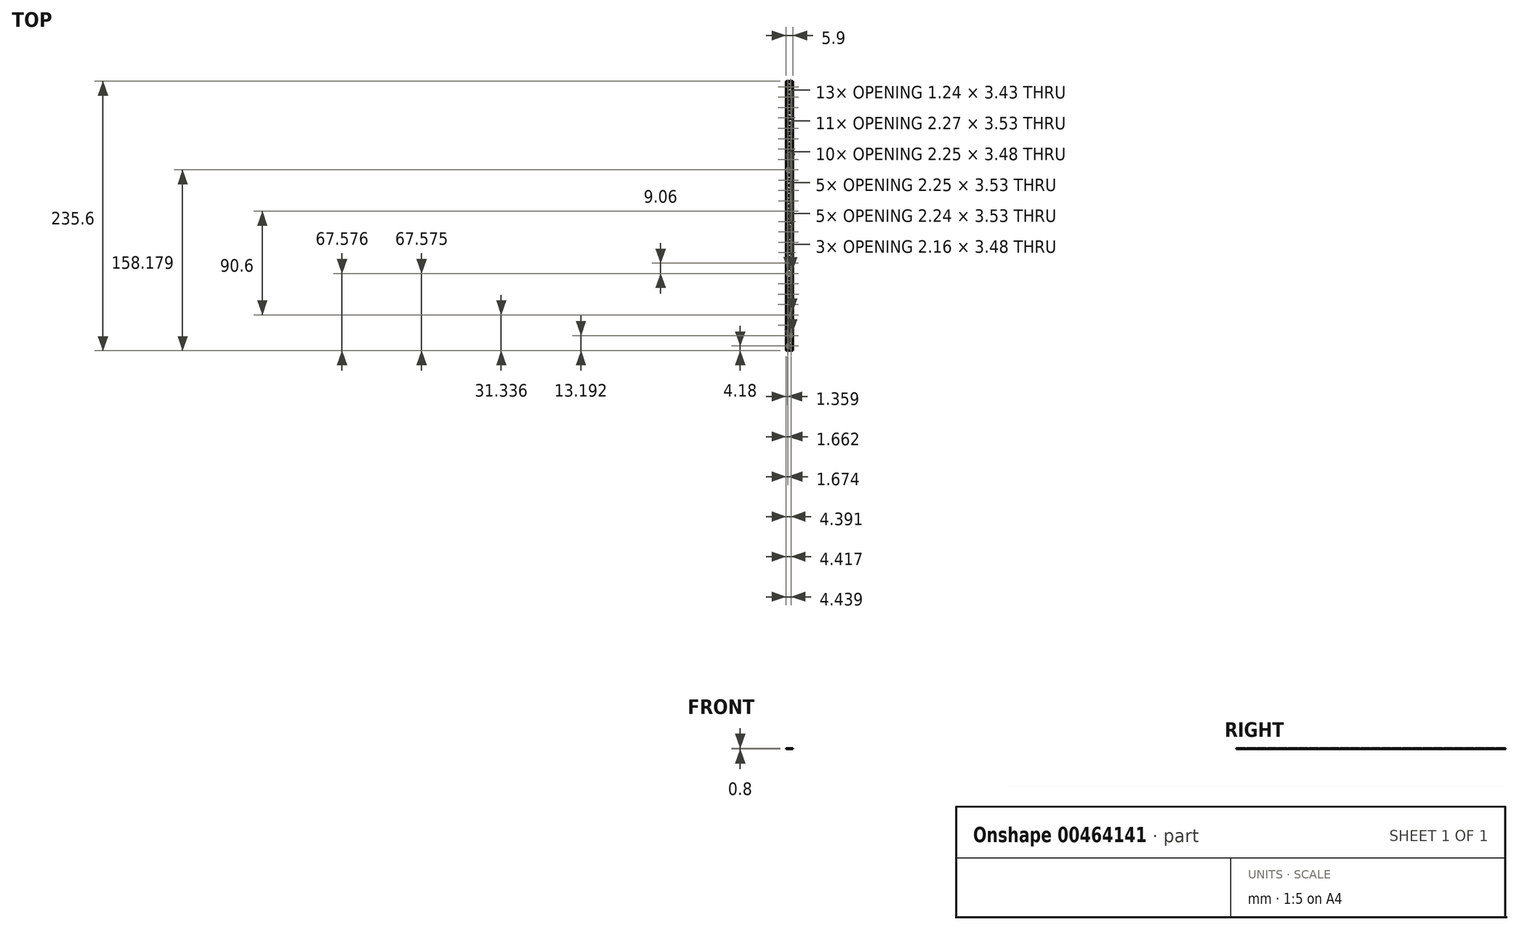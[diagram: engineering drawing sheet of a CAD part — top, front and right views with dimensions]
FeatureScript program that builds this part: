
annotation { "Feature Type Name" : "Feature", "Feature Type Description" : "" }
export const myFeature = defineFeature(function(context is Context, id is Id, definition is map)
    precondition{}
    {
        {
            var Q0;
            Q0=qCreatedBy(makeId("Top.planeOp"),FACE);
            var sketch = newSketch(context, id + "F0", { "sketchPlane" : qUnion([Q0])});
            skLineSegment(sketch, "E0.bottom", {"start": v(0, 0) * mm, "end": v(7.5, 0) * mm});
            skLineSegment(sketch, "E0.top", {"start": v(0, -235.6) * mm, "end": v(7.5, -235.6) * mm});
            skLineSegment(sketch, "E0.left", {"start": v(0, 0) * mm, "end": v(0, -235.6) * mm});
            skLineSegment(sketch, "E0.right", {"start": v(7.5, 0) * mm, "end": v(7.5, -235.6) * mm});
            skLineSegment(sketch, "E1.bottom", {"start": v(0.8, -0.8) * mm, "end": v(6.7, -0.8) * mm});
            skLineSegment(sketch, "E1.top", {"start": v(0.8, -9.06) * mm, "end": v(6.7, -9.06) * mm});
            skLineSegment(sketch, "E1.left", {"start": v(0.8, -0.8) * mm, "end": v(0.8, -9.06) * mm});
            skLineSegment(sketch, "E1.right", {"start": v(6.7, -0.8) * mm, "end": v(6.7, -9.06) * mm});
            skText(sketch, "E2", { "text": "01", "fontName": "OpenSans-Regular.ttf"});
            skPoint(sketch, "E3", {"position": v(1.1, -3.2) * mm});
            skPoint(sketch, "E4", {"position": v(5.84, -6.66) * mm});
            skLineSegment(sketch, "E5.0.1.0", {"start": v(0.8, -9.86) * mm, "end": v(6.7, -9.86) * mm});
            skLineSegment(sketch, "E5.0.1.1", {"start": v(0.8, -9.86) * mm, "end": v(0.8, -18.12) * mm});
            skLineSegment(sketch, "E5.0.1.2", {"start": v(0.8, -18.12) * mm, "end": v(6.7, -18.12) * mm});
            skLineSegment(sketch, "E5.0.1.3", {"start": v(6.7, -9.86) * mm, "end": v(6.7, -18.12) * mm});
            skPoint(sketch, "E5.0.1.4", {"position": v(1.1, -12.26) * mm});
            skPoint(sketch, "E5.0.1.5", {"position": v(5.84, -15.72) * mm});
            skLineSegment(sketch, "E5.0.2.0", {"start": v(0.8, -18.92) * mm, "end": v(6.7, -18.92) * mm});
            skLineSegment(sketch, "E5.0.2.1", {"start": v(0.8, -18.92) * mm, "end": v(0.8, -27.18) * mm});
            skLineSegment(sketch, "E5.0.2.2", {"start": v(0.8, -27.18) * mm, "end": v(6.7, -27.18) * mm});
            skLineSegment(sketch, "E5.0.2.3", {"start": v(6.7, -18.92) * mm, "end": v(6.7, -27.18) * mm});
            skPoint(sketch, "E5.0.2.4", {"position": v(1.1, -21.32) * mm});
            skPoint(sketch, "E5.0.2.5", {"position": v(5.84, -24.78) * mm});
            skLineSegment(sketch, "E5.0.3.0", {"start": v(0.8, -27.98) * mm, "end": v(6.7, -27.98) * mm});
            skLineSegment(sketch, "E5.0.3.1", {"start": v(0.8, -27.98) * mm, "end": v(0.8, -36.24) * mm});
            skLineSegment(sketch, "E5.0.3.2", {"start": v(0.8, -36.24) * mm, "end": v(6.7, -36.24) * mm});
            skLineSegment(sketch, "E5.0.3.3", {"start": v(6.7, -27.98) * mm, "end": v(6.7, -36.24) * mm});
            skPoint(sketch, "E5.0.3.4", {"position": v(1.1, -30.38) * mm});
            skPoint(sketch, "E5.0.3.5", {"position": v(5.84, -33.84) * mm});
            skLineSegment(sketch, "E5.0.4.0", {"start": v(0.8, -37.04) * mm, "end": v(6.7, -37.04) * mm});
            skLineSegment(sketch, "E5.0.4.1", {"start": v(0.8, -37.04) * mm, "end": v(0.8, -45.3) * mm});
            skLineSegment(sketch, "E5.0.4.2", {"start": v(0.8, -45.3) * mm, "end": v(6.7, -45.3) * mm});
            skLineSegment(sketch, "E5.0.4.3", {"start": v(6.7, -37.04) * mm, "end": v(6.7, -45.3) * mm});
            skPoint(sketch, "E5.0.4.4", {"position": v(1.1, -39.44) * mm});
            skPoint(sketch, "E5.0.4.5", {"position": v(5.84, -42.9) * mm});
            skLineSegment(sketch, "E5.0.5.0", {"start": v(0.8, -46.1) * mm, "end": v(6.7, -46.1) * mm});
            skLineSegment(sketch, "E5.0.5.1", {"start": v(0.8, -46.1) * mm, "end": v(0.8, -54.36) * mm});
            skLineSegment(sketch, "E5.0.5.2", {"start": v(0.8, -54.36) * mm, "end": v(6.7, -54.36) * mm});
            skLineSegment(sketch, "E5.0.5.3", {"start": v(6.7, -46.1) * mm, "end": v(6.7, -54.36) * mm});
            skPoint(sketch, "E5.0.5.4", {"position": v(1.1, -48.5) * mm});
            skPoint(sketch, "E5.0.5.5", {"position": v(5.84, -51.96) * mm});
            skLineSegment(sketch, "E5.0.6.0", {"start": v(0.8, -55.16) * mm, "end": v(6.7, -55.16) * mm});
            skLineSegment(sketch, "E5.0.6.1", {"start": v(0.8, -55.16) * mm, "end": v(0.8, -63.42) * mm});
            skLineSegment(sketch, "E5.0.6.2", {"start": v(0.8, -63.42) * mm, "end": v(6.7, -63.42) * mm});
            skLineSegment(sketch, "E5.0.6.3", {"start": v(6.7, -55.16) * mm, "end": v(6.7, -63.42) * mm});
            skPoint(sketch, "E5.0.6.4", {"position": v(1.1, -57.56) * mm});
            skPoint(sketch, "E5.0.6.5", {"position": v(5.84, -61.02) * mm});
            skLineSegment(sketch, "E5.0.7.0", {"start": v(0.8, -64.22) * mm, "end": v(6.7, -64.22) * mm});
            skLineSegment(sketch, "E5.0.7.1", {"start": v(0.8, -64.22) * mm, "end": v(0.8, -72.48) * mm});
            skLineSegment(sketch, "E5.0.7.2", {"start": v(0.8, -72.48) * mm, "end": v(6.7, -72.48) * mm});
            skLineSegment(sketch, "E5.0.7.3", {"start": v(6.7, -64.22) * mm, "end": v(6.7, -72.48) * mm});
            skPoint(sketch, "E5.0.7.4", {"position": v(1.1, -66.62) * mm});
            skPoint(sketch, "E5.0.7.5", {"position": v(5.84, -70.08) * mm});
            skLineSegment(sketch, "E5.0.8.0", {"start": v(0.8, -73.28) * mm, "end": v(6.7, -73.28) * mm});
            skLineSegment(sketch, "E5.0.8.1", {"start": v(0.8, -73.28) * mm, "end": v(0.8, -81.54) * mm});
            skLineSegment(sketch, "E5.0.8.2", {"start": v(0.8, -81.54) * mm, "end": v(6.7, -81.54) * mm});
            skLineSegment(sketch, "E5.0.8.3", {"start": v(6.7, -73.28) * mm, "end": v(6.7, -81.54) * mm});
            skPoint(sketch, "E5.0.8.4", {"position": v(1.1, -75.68) * mm});
            skPoint(sketch, "E5.0.8.5", {"position": v(5.84, -79.14) * mm});
            skLineSegment(sketch, "E5.0.9.0", {"start": v(0.8, -82.34) * mm, "end": v(6.7, -82.34) * mm});
            skLineSegment(sketch, "E5.0.9.1", {"start": v(0.8, -82.34) * mm, "end": v(0.8, -90.6) * mm});
            skLineSegment(sketch, "E5.0.9.2", {"start": v(0.8, -90.6) * mm, "end": v(6.7, -90.6) * mm});
            skLineSegment(sketch, "E5.0.9.3", {"start": v(6.7, -82.34) * mm, "end": v(6.7, -90.6) * mm});
            skPoint(sketch, "E5.0.9.4", {"position": v(1.1, -84.74) * mm});
            skPoint(sketch, "E5.0.9.5", {"position": v(5.84, -88.2) * mm});
            skLineSegment(sketch, "E5.0.10.0", {"start": v(0.8, -91.4) * mm, "end": v(6.7, -91.4) * mm});
            skLineSegment(sketch, "E5.0.10.1", {"start": v(0.8, -91.4) * mm, "end": v(0.8, -99.66) * mm});
            skLineSegment(sketch, "E5.0.10.2", {"start": v(0.8, -99.66) * mm, "end": v(6.7, -99.66) * mm});
            skLineSegment(sketch, "E5.0.10.3", {"start": v(6.7, -91.4) * mm, "end": v(6.7, -99.66) * mm});
            skPoint(sketch, "E5.0.10.4", {"position": v(1.1, -93.8) * mm});
            skPoint(sketch, "E5.0.10.5", {"position": v(5.84, -97.26) * mm});
            skLineSegment(sketch, "E5.0.11.0", {"start": v(0.8, -100.46) * mm, "end": v(6.7, -100.46) * mm});
            skLineSegment(sketch, "E5.0.11.1", {"start": v(0.8, -100.46) * mm, "end": v(0.8, -108.72) * mm});
            skLineSegment(sketch, "E5.0.11.2", {"start": v(0.8, -108.72) * mm, "end": v(6.7, -108.72) * mm});
            skLineSegment(sketch, "E5.0.11.3", {"start": v(6.7, -100.46) * mm, "end": v(6.7, -108.72) * mm});
            skPoint(sketch, "E5.0.11.4", {"position": v(1.1, -102.86) * mm});
            skPoint(sketch, "E5.0.11.5", {"position": v(5.84, -106.32) * mm});
            skLineSegment(sketch, "E5.0.12.0", {"start": v(0.8, -109.52) * mm, "end": v(6.7, -109.52) * mm});
            skLineSegment(sketch, "E5.0.12.1", {"start": v(0.8, -109.52) * mm, "end": v(0.8, -117.78) * mm});
            skLineSegment(sketch, "E5.0.12.2", {"start": v(0.8, -117.78) * mm, "end": v(6.7, -117.78) * mm});
            skLineSegment(sketch, "E5.0.12.3", {"start": v(6.7, -109.52) * mm, "end": v(6.7, -117.78) * mm});
            skPoint(sketch, "E5.0.12.4", {"position": v(1.1, -111.92) * mm});
            skPoint(sketch, "E5.0.12.5", {"position": v(5.84, -115.38) * mm});
            skLineSegment(sketch, "E5.0.13.0", {"start": v(0.8, -118.58) * mm, "end": v(6.7, -118.58) * mm});
            skLineSegment(sketch, "E5.0.13.1", {"start": v(0.8, -118.58) * mm, "end": v(0.8, -126.84) * mm});
            skLineSegment(sketch, "E5.0.13.2", {"start": v(0.8, -126.84) * mm, "end": v(6.7, -126.84) * mm});
            skLineSegment(sketch, "E5.0.13.3", {"start": v(6.7, -118.58) * mm, "end": v(6.7, -126.84) * mm});
            skPoint(sketch, "E5.0.13.4", {"position": v(1.1, -120.98) * mm});
            skPoint(sketch, "E5.0.13.5", {"position": v(5.84, -124.44) * mm});
            skLineSegment(sketch, "E5.0.14.0", {"start": v(0.8, -127.64) * mm, "end": v(6.7, -127.64) * mm});
            skLineSegment(sketch, "E5.0.14.1", {"start": v(0.8, -127.64) * mm, "end": v(0.8, -135.9) * mm});
            skLineSegment(sketch, "E5.0.14.2", {"start": v(0.8, -135.9) * mm, "end": v(6.7, -135.9) * mm});
            skLineSegment(sketch, "E5.0.14.3", {"start": v(6.7, -127.64) * mm, "end": v(6.7, -135.9) * mm});
            skPoint(sketch, "E5.0.14.4", {"position": v(1.1, -130.04) * mm});
            skPoint(sketch, "E5.0.14.5", {"position": v(5.84, -133.5) * mm});
            skLineSegment(sketch, "E5.0.15.0", {"start": v(0.8, -136.7) * mm, "end": v(6.7, -136.7) * mm});
            skLineSegment(sketch, "E5.0.15.1", {"start": v(0.8, -136.7) * mm, "end": v(0.8, -144.96) * mm});
            skLineSegment(sketch, "E5.0.15.2", {"start": v(0.8, -144.96) * mm, "end": v(6.7, -144.96) * mm});
            skLineSegment(sketch, "E5.0.15.3", {"start": v(6.7, -136.7) * mm, "end": v(6.7, -144.96) * mm});
            skPoint(sketch, "E5.0.15.4", {"position": v(1.1, -139.1) * mm});
            skPoint(sketch, "E5.0.15.5", {"position": v(5.84, -142.56) * mm});
            skLineSegment(sketch, "E5.0.16.0", {"start": v(0.8, -145.76) * mm, "end": v(6.7, -145.76) * mm});
            skLineSegment(sketch, "E5.0.16.1", {"start": v(0.8, -145.76) * mm, "end": v(0.8, -154.02) * mm});
            skLineSegment(sketch, "E5.0.16.2", {"start": v(0.8, -154.02) * mm, "end": v(6.7, -154.02) * mm});
            skLineSegment(sketch, "E5.0.16.3", {"start": v(6.7, -145.76) * mm, "end": v(6.7, -154.02) * mm});
            skPoint(sketch, "E5.0.16.4", {"position": v(1.1, -148.16) * mm});
            skPoint(sketch, "E5.0.16.5", {"position": v(5.84, -151.62) * mm});
            skLineSegment(sketch, "E5.0.17.0", {"start": v(0.8, -154.82) * mm, "end": v(6.7, -154.82) * mm});
            skLineSegment(sketch, "E5.0.17.1", {"start": v(0.8, -154.82) * mm, "end": v(0.8, -163.08) * mm});
            skLineSegment(sketch, "E5.0.17.2", {"start": v(0.8, -163.08) * mm, "end": v(6.7, -163.08) * mm});
            skLineSegment(sketch, "E5.0.17.3", {"start": v(6.7, -154.82) * mm, "end": v(6.7, -163.08) * mm});
            skPoint(sketch, "E5.0.17.4", {"position": v(1.1, -157.22) * mm});
            skPoint(sketch, "E5.0.17.5", {"position": v(5.84, -160.68) * mm});
            skLineSegment(sketch, "E5.0.18.0", {"start": v(0.8, -163.88) * mm, "end": v(6.7, -163.88) * mm});
            skLineSegment(sketch, "E5.0.18.1", {"start": v(0.8, -163.88) * mm, "end": v(0.8, -172.14) * mm});
            skLineSegment(sketch, "E5.0.18.2", {"start": v(0.8, -172.14) * mm, "end": v(6.7, -172.14) * mm});
            skLineSegment(sketch, "E5.0.18.3", {"start": v(6.7, -163.88) * mm, "end": v(6.7, -172.14) * mm});
            skPoint(sketch, "E5.0.18.4", {"position": v(1.1, -166.28) * mm});
            skPoint(sketch, "E5.0.18.5", {"position": v(5.84, -169.74) * mm});
            skLineSegment(sketch, "E5.0.19.0", {"start": v(0.8, -172.94) * mm, "end": v(6.7, -172.94) * mm});
            skLineSegment(sketch, "E5.0.19.1", {"start": v(0.8, -172.94) * mm, "end": v(0.8, -181.2) * mm});
            skLineSegment(sketch, "E5.0.19.2", {"start": v(0.8, -181.2) * mm, "end": v(6.7, -181.2) * mm});
            skLineSegment(sketch, "E5.0.19.3", {"start": v(6.7, -172.94) * mm, "end": v(6.7, -181.2) * mm});
            skPoint(sketch, "E5.0.19.4", {"position": v(1.1, -175.34) * mm});
            skPoint(sketch, "E5.0.19.5", {"position": v(5.84, -178.8) * mm});
            skLineSegment(sketch, "E5.0.20.0", {"start": v(0.8, -182) * mm, "end": v(6.7, -182) * mm});
            skLineSegment(sketch, "E5.0.20.1", {"start": v(0.8, -182) * mm, "end": v(0.8, -190.26) * mm});
            skLineSegment(sketch, "E5.0.20.2", {"start": v(0.8, -190.26) * mm, "end": v(6.7, -190.26) * mm});
            skLineSegment(sketch, "E5.0.20.3", {"start": v(6.7, -182) * mm, "end": v(6.7, -190.26) * mm});
            skPoint(sketch, "E5.0.20.4", {"position": v(1.1, -184.4) * mm});
            skPoint(sketch, "E5.0.20.5", {"position": v(5.84, -187.86) * mm});
            skLineSegment(sketch, "E5.0.21.0", {"start": v(0.8, -191.06) * mm, "end": v(6.7, -191.06) * mm});
            skLineSegment(sketch, "E5.0.21.1", {"start": v(0.8, -191.06) * mm, "end": v(0.8, -199.32) * mm});
            skLineSegment(sketch, "E5.0.21.2", {"start": v(0.8, -199.32) * mm, "end": v(6.7, -199.32) * mm});
            skLineSegment(sketch, "E5.0.21.3", {"start": v(6.7, -191.06) * mm, "end": v(6.7, -199.32) * mm});
            skPoint(sketch, "E5.0.21.4", {"position": v(1.1, -193.46) * mm});
            skPoint(sketch, "E5.0.21.5", {"position": v(5.84, -196.92) * mm});
            skLineSegment(sketch, "E5.0.22.0", {"start": v(0.8, -200.12) * mm, "end": v(6.7, -200.12) * mm});
            skLineSegment(sketch, "E5.0.22.1", {"start": v(0.8, -200.12) * mm, "end": v(0.8, -208.38) * mm});
            skLineSegment(sketch, "E5.0.22.2", {"start": v(0.8, -208.38) * mm, "end": v(6.7, -208.38) * mm});
            skLineSegment(sketch, "E5.0.22.3", {"start": v(6.7, -200.12) * mm, "end": v(6.7, -208.38) * mm});
            skPoint(sketch, "E5.0.22.4", {"position": v(1.1, -202.52) * mm});
            skPoint(sketch, "E5.0.22.5", {"position": v(5.84, -205.98) * mm});
            skLineSegment(sketch, "E5.0.23.0", {"start": v(0.8, -209.18) * mm, "end": v(6.7, -209.18) * mm});
            skLineSegment(sketch, "E5.0.23.1", {"start": v(0.8, -209.18) * mm, "end": v(0.8, -217.44) * mm});
            skLineSegment(sketch, "E5.0.23.2", {"start": v(0.8, -217.44) * mm, "end": v(6.7, -217.44) * mm});
            skLineSegment(sketch, "E5.0.23.3", {"start": v(6.7, -209.18) * mm, "end": v(6.7, -217.44) * mm});
            skPoint(sketch, "E5.0.23.4", {"position": v(1.1, -211.58) * mm});
            skPoint(sketch, "E5.0.23.5", {"position": v(5.84, -215.04) * mm});
            skLineSegment(sketch, "E5.0.24.0", {"start": v(0.8, -218.24) * mm, "end": v(6.7, -218.24) * mm});
            skLineSegment(sketch, "E5.0.24.1", {"start": v(0.8, -218.24) * mm, "end": v(0.8, -226.5) * mm});
            skLineSegment(sketch, "E5.0.24.2", {"start": v(0.8, -226.5) * mm, "end": v(6.7, -226.5) * mm});
            skLineSegment(sketch, "E5.0.24.3", {"start": v(6.7, -218.24) * mm, "end": v(6.7, -226.5) * mm});
            skPoint(sketch, "E5.0.24.4", {"position": v(1.1, -220.64) * mm});
            skPoint(sketch, "E5.0.24.5", {"position": v(5.84, -224.1) * mm});
            skLineSegment(sketch, "E5.0.25.0", {"start": v(0.8, -227.3) * mm, "end": v(6.7, -227.3) * mm});
            skLineSegment(sketch, "E5.0.25.1", {"start": v(0.8, -227.3) * mm, "end": v(0.8, -235.56) * mm});
            skLineSegment(sketch, "E5.0.25.2", {"start": v(0.8, -235.56) * mm, "end": v(6.7, -235.56) * mm});
            skLineSegment(sketch, "E5.0.25.3", {"start": v(6.7, -227.3) * mm, "end": v(6.7, -235.56) * mm});
            skPoint(sketch, "E5.0.25.4", {"position": v(1.1, -229.7) * mm});
            skPoint(sketch, "E5.0.25.5", {"position": v(5.84, -233.16) * mm});
            skLineSegment(sketch, "E5.direction1", {"start": v(0.8, -9.06) * mm, "end": v(25.53, -9.06) * mm, "construction": true});
            skLineSegment(sketch, "E5.direction2", {"start": v(0.8, -9.06) * mm, "end": v(0.8, -18.12) * mm, "construction": true});
            skText(sketch, "E6", { "text": "02", "fontName": "OpenSans-Regular.ttf"});
            skText(sketch, "E7", { "text": "03", "fontName": "OpenSans-Regular.ttf"});
            skText(sketch, "E8", { "text": "04", "fontName": "OpenSans-Regular.ttf"});
            skText(sketch, "E9", { "text": "05", "fontName": "OpenSans-Regular.ttf"});
            skText(sketch, "E10", { "text": "06", "fontName": "OpenSans-Regular.ttf"});
            skText(sketch, "E11", { "text": "07", "fontName": "OpenSans-Regular.ttf"});
            skText(sketch, "E12", { "text": "08", "fontName": "OpenSans-Regular.ttf"});
            skText(sketch, "E13", { "text": "09", "fontName": "OpenSans-Regular.ttf"});
            skText(sketch, "E14", { "text": "10", "fontName": "OpenSans-Regular.ttf"});
            skText(sketch, "E15", { "text": "11", "fontName": "OpenSans-Regular.ttf"});
            skText(sketch, "E16", { "text": "12", "fontName": "OpenSans-Regular.ttf"});
            skText(sketch, "E17", { "text": "13", "fontName": "OpenSans-Regular.ttf"});
            skText(sketch, "E18", { "text": "14", "fontName": "OpenSans-Regular.ttf"});
            skText(sketch, "E19", { "text": "15", "fontName": "OpenSans-Regular.ttf"});
            skText(sketch, "E20", { "text": "16", "fontName": "OpenSans-Regular.ttf"});
            skText(sketch, "E21", { "text": "17", "fontName": "OpenSans-Regular.ttf"});
            skText(sketch, "E22", { "text": "18", "fontName": "OpenSans-Regular.ttf"});
            skText(sketch, "E23", { "text": "19", "fontName": "OpenSans-Regular.ttf"});
            skText(sketch, "E24", { "text": "20", "fontName": "OpenSans-Regular.ttf"});
            skText(sketch, "E25", { "text": "21", "fontName": "OpenSans-Regular.ttf"});
            skText(sketch, "E26", { "text": "22", "fontName": "OpenSans-Regular.ttf"});
            skText(sketch, "E27", { "text": "23", "fontName": "OpenSans-Regular.ttf"});
            skText(sketch, "E28", { "text": "24", "fontName": "OpenSans-Regular.ttf"});
            skText(sketch, "E29", { "text": "25", "fontName": "OpenSans-Regular.ttf"});
            skText(sketch, "E30", { "text": "26", "fontName": "OpenSans-Regular.ttf"});
            const initialGuessF0  = {"E2": [0.0011, -0.00666, 1, 0, 0.00346], "E6": [0.0011, -0.01572, 1, 0, 0.00346], "E7": [0.0011, -0.02478, 1, 0, 0.00346], "E8": [0.0011, -0.03384, 1, 0, 0.00346], "E9": [0.0011, -0.0429, 1, 0, 0.00346], "E10": [0.0011, -0.05196, 1, 0, 0.00346], "E11": [0.0011, -0.06102, 1, 0, 0.00346], "E12": [0.0011, -0.07008, 1, 0, 0.00346], "E13": [0.0011, -0.07914, 1, 0, 0.00346], "E14": [0.0011, -0.0882, 1, 0, 0.00346], "E15": [0.0011, -0.09726, 1, 0, 0.00346], "E16": [0.0011, -0.10632, 1, 0, 0.00346], "E17": [0.0011, -0.11538, 1, 0, 0.00346], "E18": [0.0011, -0.12444, 1, 0, 0.00346], "E19": [0.0011, -0.1335, 1, 0, 0.00346], "E20": [0.0011, -0.14256, 1, 0, 0.00346], "E21": [0.0011, -0.15162, 1, 0, 0.00346], "E22": [0.0011, -0.16068, 1, 0, 0.00346], "E23": [0.0011, -0.16974, 1, 0, 0.00346], "E24": [0.0011, -0.1788, 1, 0, 0.00346], "E25": [0.0011, -0.18786, 1, 0, 0.00346], "E26": [0.0011, -0.19692, 1, 0, 0.00346], "E27": [0.0011, -0.20598, 1, 0, 0.00346], "E28": [0.0011, -0.21504, 1, 0, 0.00346], "E29": [0.0011, -0.2241, 1, 0, 0.00346], "E30": [0.0011, -0.23316, 1, 0, 0.00346]};
            skSetInitialGuess(sketch, initialGuessF0);
            skSolve(sketch);
        }
        {
            var Q0;
            Q0=makeQuery(id+"F0.imprint","IMPRINT",FACE,{"disambiguationData":[TD([[makeQuery(id+"F0.imprint","IMPRINT",EDGE,{"derivedFrom":sQuery(id+"F0.wireOp",EDGE,"E1.bottom")}),-1.0]])]});
            extrude(context, id + "F1", {"entities" : qUnion([Q0]), "depth" : .4 * mm});
        }
        {
            var Q0;
            Q0=makeQuery(id+"F0.imprint","IMPRINT",FACE,{"disambiguationData":[TD([[makeQuery(id+"F0.imprint","IMPRINT",EDGE,{"derivedFrom":sQuery(id+"F0.wireOp",EDGE,"E2.sketch_text.stroke-8")}),1.0]])]});
            var Q1;
            Q1=makeQuery(id+"F0.imprint","IMPRINT",FACE,{"disambiguationData":[TD([[makeQuery(id+"F0.imprint","IMPRINT",EDGE,{"derivedFrom":sQuery(id+"F0.wireOp",EDGE,"E5.0.1.0")}),-1.0]])]});
            var Q2;
            Q2=makeQuery(id+"F0.imprint","IMPRINT",FACE,{"disambiguationData":[TD([[makeQuery(id+"F0.imprint","IMPRINT",EDGE,{"derivedFrom":sQuery(id+"F0.wireOp",EDGE,"E6.sketch_text.stroke-8")}),1.0]])]});
            var Q3;
            Q3=makeQuery(id+"F0.imprint","IMPRINT",FACE,{"disambiguationData":[TD([[makeQuery(id+"F0.imprint","IMPRINT",EDGE,{"derivedFrom":sQuery(id+"F0.wireOp",EDGE,"E5.0.2.0")}),-1.0]])]});
            var Q4;
            Q4=makeQuery(id+"F0.imprint","IMPRINT",FACE,{"disambiguationData":[TD([[makeQuery(id+"F0.imprint","IMPRINT",EDGE,{"derivedFrom":sQuery(id+"F0.wireOp",EDGE,"E7.sketch_text.stroke-8")}),1.0]])]});
            var Q5;
            Q5=makeQuery(id+"F0.imprint","IMPRINT",FACE,{"disambiguationData":[TD([[makeQuery(id+"F0.imprint","IMPRINT",EDGE,{"derivedFrom":sQuery(id+"F0.wireOp",EDGE,"E5.0.3.0")}),-1.0]])]});
            var Q6;
            Q6=makeQuery(id+"F0.imprint","IMPRINT",FACE,{"disambiguationData":[TD([[makeQuery(id+"F0.imprint","IMPRINT",EDGE,{"derivedFrom":sQuery(id+"F0.wireOp",EDGE,"E8.sketch_text.stroke-8")}),1.0]])]});
            var Q7;
            Q7=makeQuery(id+"F0.imprint","IMPRINT",FACE,{"disambiguationData":[TD([[makeQuery(id+"F0.imprint","IMPRINT",EDGE,{"derivedFrom":sQuery(id+"F0.wireOp",EDGE,"E8.sketch_text.stroke-27")}),1.0]])]});
            var Q8;
            Q8=makeQuery(id+"F0.imprint","IMPRINT",FACE,{"disambiguationData":[TD([[makeQuery(id+"F0.imprint","IMPRINT",EDGE,{"derivedFrom":sQuery(id+"F0.wireOp",EDGE,"E5.0.4.0")}),-1.0]])]});
            var Q9;
            Q9=makeQuery(id+"F0.imprint","IMPRINT",FACE,{"disambiguationData":[TD([[makeQuery(id+"F0.imprint","IMPRINT",EDGE,{"derivedFrom":sQuery(id+"F0.wireOp",EDGE,"E9.sketch_text.stroke-8")}),1.0]])]});
            var Q10;
            Q10=makeQuery(id+"F0.imprint","IMPRINT",FACE,{"disambiguationData":[TD([[makeQuery(id+"F0.imprint","IMPRINT",EDGE,{"derivedFrom":sQuery(id+"F0.wireOp",EDGE,"E5.0.5.0")}),-1.0]])]});
            var Q11;
            Q11=makeQuery(id+"F0.imprint","IMPRINT",FACE,{"disambiguationData":[TD([[makeQuery(id+"F0.imprint","IMPRINT",EDGE,{"derivedFrom":sQuery(id+"F0.wireOp",EDGE,"E10.sketch_text.stroke-8")}),1.0]])]});
            var Q12;
            Q12=makeQuery(id+"F0.imprint","IMPRINT",FACE,{"disambiguationData":[TD([[makeQuery(id+"F0.imprint","IMPRINT",EDGE,{"derivedFrom":sQuery(id+"F0.wireOp",EDGE,"E10.sketch_text.stroke-31")}),1.0]])]});
            var Q13;
            Q13=makeQuery(id+"F0.imprint","IMPRINT",FACE,{"disambiguationData":[TD([[makeQuery(id+"F0.imprint","IMPRINT",EDGE,{"derivedFrom":sQuery(id+"F0.wireOp",EDGE,"E5.0.6.0")}),-1.0]])]});
            var Q14;
            Q14=makeQuery(id+"F0.imprint","IMPRINT",FACE,{"disambiguationData":[TD([[makeQuery(id+"F0.imprint","IMPRINT",EDGE,{"derivedFrom":sQuery(id+"F0.wireOp",EDGE,"E11.sketch_text.stroke-8")}),1.0]])]});
            var Q15;
            Q15=makeQuery(id+"F0.imprint","IMPRINT",FACE,{"disambiguationData":[TD([[makeQuery(id+"F0.imprint","IMPRINT",EDGE,{"derivedFrom":sQuery(id+"F0.wireOp",EDGE,"E5.0.7.0")}),-1.0]])]});
            var Q16;
            Q16=makeQuery(id+"F0.imprint","IMPRINT",FACE,{"disambiguationData":[TD([[makeQuery(id+"F0.imprint","IMPRINT",EDGE,{"derivedFrom":sQuery(id+"F0.wireOp",EDGE,"E12.sketch_text.stroke-8")}),1.0]])]});
            var Q17;
            Q17=makeQuery(id+"F0.imprint","IMPRINT",FACE,{"disambiguationData":[TD([[makeQuery(id+"F0.imprint","IMPRINT",EDGE,{"derivedFrom":sQuery(id+"F0.wireOp",EDGE,"E12.sketch_text.stroke-39")}),1.0]])]});
            var Q18;
            Q18=makeQuery(id+"F0.imprint","IMPRINT",FACE,{"disambiguationData":[TD([[makeQuery(id+"F0.imprint","IMPRINT",EDGE,{"derivedFrom":sQuery(id+"F0.wireOp",EDGE,"E12.sketch_text.stroke-31")}),1.0]])]});
            var Q19;
            Q19=makeQuery(id+"F0.imprint","IMPRINT",FACE,{"disambiguationData":[TD([[makeQuery(id+"F0.imprint","IMPRINT",EDGE,{"derivedFrom":sQuery(id+"F0.wireOp",EDGE,"E5.0.8.0")}),-1.0]])]});
            var Q20;
            Q20=makeQuery(id+"F0.imprint","IMPRINT",FACE,{"disambiguationData":[TD([[makeQuery(id+"F0.imprint","IMPRINT",EDGE,{"derivedFrom":sQuery(id+"F0.wireOp",EDGE,"E13.sketch_text.stroke-8")}),1.0]])]});
            var Q21;
            Q21=makeQuery(id+"F0.imprint","IMPRINT",FACE,{"disambiguationData":[TD([[makeQuery(id+"F0.imprint","IMPRINT",EDGE,{"derivedFrom":sQuery(id+"F0.wireOp",EDGE,"E13.sketch_text.stroke-32")}),1.0]])]});
            var Q22;
            Q22=makeQuery(id+"F0.imprint","IMPRINT",FACE,{"disambiguationData":[TD([[makeQuery(id+"F0.imprint","IMPRINT",EDGE,{"derivedFrom":sQuery(id+"F0.wireOp",EDGE,"E5.0.9.0")}),-1.0]])]});
            var Q23;
            Q23=makeQuery(id+"F0.imprint","IMPRINT",FACE,{"disambiguationData":[TD([[makeQuery(id+"F0.imprint","IMPRINT",EDGE,{"derivedFrom":sQuery(id+"F0.wireOp",EDGE,"E14.sketch_text.stroke-17")}),1.0]])]});
            var Q24;
            Q24=makeQuery(id+"F0.imprint","IMPRINT",FACE,{"disambiguationData":[TD([[makeQuery(id+"F0.imprint","IMPRINT",EDGE,{"derivedFrom":sQuery(id+"F0.wireOp",EDGE,"E5.0.10.0")}),-1.0]])]});
            var Q25;
            Q25=makeQuery(id+"F0.imprint","IMPRINT",FACE,{"disambiguationData":[TD([[makeQuery(id+"F0.imprint","IMPRINT",EDGE,{"derivedFrom":sQuery(id+"F0.wireOp",EDGE,"E5.0.11.0")}),-1.0]])]});
            var Q26;
            Q26=makeQuery(id+"F0.imprint","IMPRINT",FACE,{"disambiguationData":[TD([[makeQuery(id+"F0.imprint","IMPRINT",EDGE,{"derivedFrom":sQuery(id+"F0.wireOp",EDGE,"E5.0.12.0")}),-1.0]])]});
            var Q27;
            Q27=makeQuery(id+"F0.imprint","IMPRINT",FACE,{"disambiguationData":[TD([[makeQuery(id+"F0.imprint","IMPRINT",EDGE,{"derivedFrom":sQuery(id+"F0.wireOp",EDGE,"E5.0.13.0")}),-1.0]])]});
            var Q28;
            Q28=makeQuery(id+"F0.imprint","IMPRINT",FACE,{"disambiguationData":[TD([[makeQuery(id+"F0.imprint","IMPRINT",EDGE,{"derivedFrom":sQuery(id+"F0.wireOp",EDGE,"E18.sketch_text.stroke-20")}),1.0]])]});
            var Q29;
            Q29=makeQuery(id+"F0.imprint","IMPRINT",FACE,{"disambiguationData":[TD([[makeQuery(id+"F0.imprint","IMPRINT",EDGE,{"derivedFrom":sQuery(id+"F0.wireOp",EDGE,"E5.0.14.0")}),-1.0]])]});
            var Q30;
            Q30=makeQuery(id+"F0.imprint","IMPRINT",FACE,{"disambiguationData":[TD([[makeQuery(id+"F0.imprint","IMPRINT",EDGE,{"derivedFrom":sQuery(id+"F0.wireOp",EDGE,"E5.0.15.0")}),-1.0]])]});
            var Q31;
            Q31=makeQuery(id+"F0.imprint","IMPRINT",FACE,{"disambiguationData":[TD([[makeQuery(id+"F0.imprint","IMPRINT",EDGE,{"derivedFrom":sQuery(id+"F0.wireOp",EDGE,"E20.sketch_text.stroke-24")}),1.0]])]});
            var Q32;
            Q32=makeQuery(id+"F0.imprint","IMPRINT",FACE,{"disambiguationData":[TD([[makeQuery(id+"F0.imprint","IMPRINT",EDGE,{"derivedFrom":sQuery(id+"F0.wireOp",EDGE,"E5.0.16.0")}),-1.0]])]});
            var Q33;
            Q33=makeQuery(id+"F0.imprint","IMPRINT",FACE,{"disambiguationData":[TD([[makeQuery(id+"F0.imprint","IMPRINT",EDGE,{"derivedFrom":sQuery(id+"F0.wireOp",EDGE,"E5.0.17.0")}),-1.0]])]});
            var Q34;
            Q34=makeQuery(id+"F0.imprint","IMPRINT",FACE,{"disambiguationData":[TD([[makeQuery(id+"F0.imprint","IMPRINT",EDGE,{"derivedFrom":sQuery(id+"F0.wireOp",EDGE,"E22.sketch_text.stroke-32")}),1.0]])]});
            var Q35;
            Q35=makeQuery(id+"F0.imprint","IMPRINT",FACE,{"disambiguationData":[TD([[makeQuery(id+"F0.imprint","IMPRINT",EDGE,{"derivedFrom":sQuery(id+"F0.wireOp",EDGE,"E22.sketch_text.stroke-24")}),1.0]])]});
            var Q36;
            Q36=makeQuery(id+"F0.imprint","IMPRINT",FACE,{"disambiguationData":[TD([[makeQuery(id+"F0.imprint","IMPRINT",EDGE,{"derivedFrom":sQuery(id+"F0.wireOp",EDGE,"E5.0.18.0")}),-1.0]])]});
            var Q37;
            Q37=makeQuery(id+"F0.imprint","IMPRINT",FACE,{"disambiguationData":[TD([[makeQuery(id+"F0.imprint","IMPRINT",EDGE,{"derivedFrom":sQuery(id+"F0.wireOp",EDGE,"E23.sketch_text.stroke-25")}),1.0]])]});
            var Q38;
            Q38=makeQuery(id+"F0.imprint","IMPRINT",FACE,{"disambiguationData":[TD([[makeQuery(id+"F0.imprint","IMPRINT",EDGE,{"derivedFrom":sQuery(id+"F0.wireOp",EDGE,"E5.0.19.0")}),-1.0]])]});
            var Q39;
            Q39=makeQuery(id+"F0.imprint","IMPRINT",FACE,{"disambiguationData":[TD([[makeQuery(id+"F0.imprint","IMPRINT",EDGE,{"derivedFrom":sQuery(id+"F0.wireOp",EDGE,"E24.sketch_text.stroke-28")}),1.0]])]});
            var Q40;
            Q40=makeQuery(id+"F0.imprint","IMPRINT",FACE,{"disambiguationData":[TD([[makeQuery(id+"F0.imprint","IMPRINT",EDGE,{"derivedFrom":sQuery(id+"F0.wireOp",EDGE,"E5.0.20.0")}),-1.0]])]});
            var Q41;
            Q41=makeQuery(id+"F0.imprint","IMPRINT",FACE,{"disambiguationData":[TD([[makeQuery(id+"F0.imprint","IMPRINT",EDGE,{"derivedFrom":sQuery(id+"F0.wireOp",EDGE,"E5.0.21.0")}),-1.0]])]});
            var Q42;
            Q42=makeQuery(id+"F0.imprint","IMPRINT",FACE,{"disambiguationData":[TD([[makeQuery(id+"F0.imprint","IMPRINT",EDGE,{"derivedFrom":sQuery(id+"F0.wireOp",EDGE,"E5.0.22.0")}),-1.0]])]});
            var Q43;
            Q43=makeQuery(id+"F0.imprint","IMPRINT",FACE,{"disambiguationData":[TD([[makeQuery(id+"F0.imprint","IMPRINT",EDGE,{"derivedFrom":sQuery(id+"F0.wireOp",EDGE,"E5.0.23.0")}),-1.0]])]});
            var Q44;
            Q44=makeQuery(id+"F0.imprint","IMPRINT",FACE,{"disambiguationData":[TD([[makeQuery(id+"F0.imprint","IMPRINT",EDGE,{"derivedFrom":sQuery(id+"F0.wireOp",EDGE,"E28.sketch_text.stroke-31")}),1.0]])]});
            var Q45;
            Q45=makeQuery(id+"F0.imprint","IMPRINT",FACE,{"disambiguationData":[TD([[makeQuery(id+"F0.imprint","IMPRINT",EDGE,{"derivedFrom":sQuery(id+"F0.wireOp",EDGE,"E5.0.24.0")}),-1.0]])]});
            var Q46;
            Q46=makeQuery(id+"F0.imprint","IMPRINT",FACE,{"disambiguationData":[TD([[makeQuery(id+"F0.imprint","IMPRINT",EDGE,{"derivedFrom":sQuery(id+"F0.wireOp",EDGE,"E5.0.25.0")}),-1.0]])]});
            var Q47;
            Q47=makeQuery(id+"F0.imprint","IMPRINT",FACE,{"disambiguationData":[TD([[makeQuery(id+"F0.imprint","IMPRINT",EDGE,{"derivedFrom":sQuery(id+"F0.wireOp",EDGE,"E30.sketch_text.stroke-35")}),1.0]])]});
            extrude(context, id + "F2", {"entities" : qUnion([Q0, Q1, Q2, Q3, Q4, Q5, Q6, Q7, Q8, Q9, Q10, Q11, Q12, Q13, Q14, Q15, Q16, Q17, Q18, Q19, Q20, Q21, Q22, Q23, Q24, Q25, Q26, Q27, Q28, Q29, Q30, Q31, Q32, Q33, Q34, Q35, Q36, Q37, Q38, Q39, Q40, Q41, Q42, Q43, Q44, Q45, Q46, Q47]), "operationType" : NewBodyOperationType.ADD, "depth" : .4 * mm});
        }
        {
            var Q0;
            Q0=qCreatedBy(makeId("Top.planeOp"),FACE);
            var sketch = newSketch(context, id + "F3", { "sketchPlane" : qUnion([Q0])});
            skLineSegment(sketch, "E31.1", {"start": v(0.8, 0) * mm, "end": v(6.7, 0) * mm});
            skLineSegment(sketch, "E31.3", {"start": v(0, -235.6) * mm, "end": v(7.5, -235.6) * mm});
            skPoint(sketch, "E31.4", {"position": v(3.75, 0) * mm});
            skLineSegment(sketch, "E32.top", {"start": v(0.8, -235.6) * mm, "end": v(6.7, -235.6) * mm});
            skLineSegment(sketch, "E33.0", {"start": v(6.7, -0.8) * mm, "end": v(6.7, -9.06) * mm});
            skPoint(sketch, "E34", {"position": v(6.7, 0) * mm});
            skLineSegment(sketch, "E35.0", {"start": v(0.8, -0.8) * mm, "end": v(0.8, -9.06) * mm});
            skPoint(sketch, "E36", {"position": v(0.8, 0) * mm});
            skLineSegment(sketch, "E37", {"start": v(6.7, 0) * mm, "end": v(6.7, -235.6) * mm});
            skLineSegment(sketch, "E38", {"start": v(0.8, 0) * mm, "end": v(0.8, -235.6) * mm});
            skPoint(sketch, "E31.2.end.orphan", {"position": v(7.5, -235.6) * mm});
            skPoint(sketch, "E31.2.start.orphan", {"position": v(7.5, 0) * mm});
            skPoint(sketch, "E31.0.end.orphan", {"position": v(0, -235.6) * mm});
            skPoint(sketch, "E31.0.start.orphan", {"position": v(0, 0) * mm});
            skSolve(sketch);
        }
        {
            var Q0;
            Q0=qSketchRegion(id+"F3",true);
            extrude(context, id + "F4", {"entities" : qUnion([Q0]), "oppositeDirection" : true, "depth" : .4 * mm});
        }
    });
